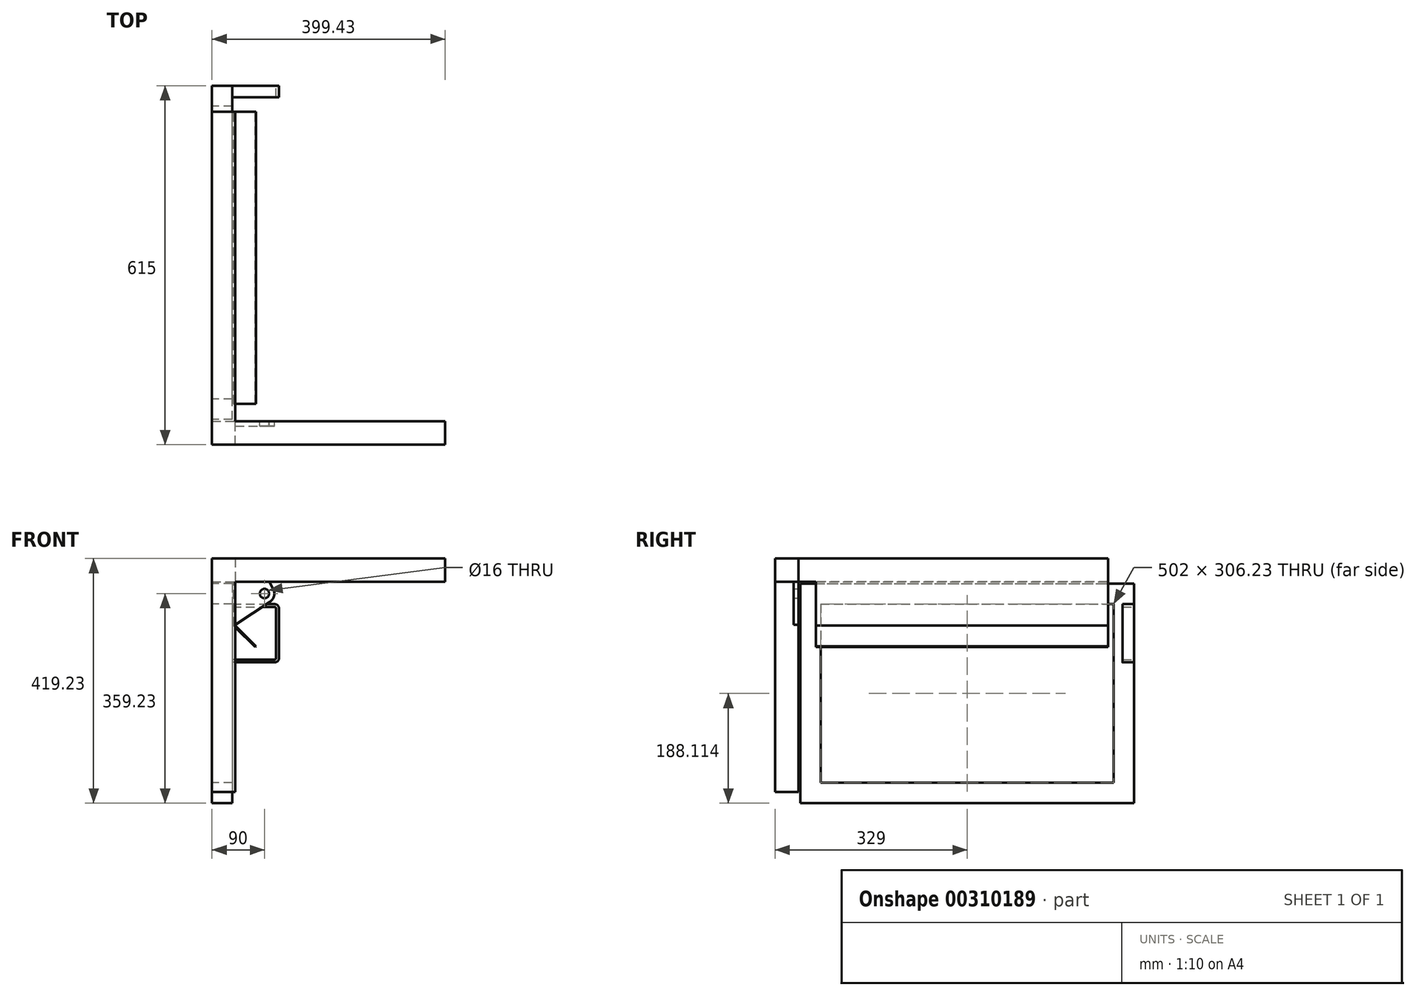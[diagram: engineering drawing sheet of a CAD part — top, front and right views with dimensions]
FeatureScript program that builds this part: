
annotation { "Feature Type Name" : "Feature", "Feature Type Description" : "" }
export const myFeature = defineFeature(function(context is Context, id is Id, definition is map)
    precondition{}
    {
        {
            var Q0;
            Q0=qCreatedBy(makeId("Front.planeOp"),FACE);
            var sketch = newSketch(context, id + "F0", { "sketchPlane" : qUnion([Q0])});
            skLineSegment(sketch, "E0.top", {"start": v(0, -400) * mm, "end": v(40, -400) * mm});
            skLineSegment(sketch, "E0.left", {"start": v(0, 0) * mm, "end": v(0, -400) * mm});
            skLineSegment(sketch, "E0.right", {"start": v(40, -40) * mm, "end": v(40, -400) * mm});
            skLineSegment(sketch, "E1.bottom", {"start": v(-0.57, 0) * mm, "end": v(399.43, 0) * mm});
            skLineSegment(sketch, "E1.top", {"start": v(40, -40) * mm, "end": v(399.43, -40) * mm});
            skLineSegment(sketch, "E1.right", {"start": v(399.43, 0) * mm, "end": v(399.43, -40) * mm});
            skSolve(sketch);
        }
        {
            var Q0;
            Q0 = qSketchRegion(id + "F0", true);
            extrude(context, id + "F1", {"entities" : qUnion([Q0]), "depth" : 40 * mm});
        }
        {
            var Q0;
            Q0=makeQuery(id+"F1.opExtrude","CAP_FACE",FACE,{"disambiguationData":[OSD([sQuery(id+"F0.wireOp",EDGE,"E0.top"),sQuery(id+"F0.wireOp",EDGE,"E0.left"),sQuery(id+"F0.wireOp",EDGE,"E0.right"),sQuery(id+"F0.wireOp",EDGE,"E1.bottom"),sQuery(id+"F0.wireOp",EDGE,"E1.top"),sQuery(id+"F0.wireOp",EDGE,"E1.right")])],"isStart":true});
            var sketch = newSketch(context, id + "F2", { "sketchPlane" : qUnion([Q0])});
            skLineSegment(sketch, "E2.bottom", {"start": v(0, 0) * mm, "end": v(-40, 0) * mm});
            skLineSegment(sketch, "E2.top", {"start": v(0, -40) * mm, "end": v(-40, -40) * mm});
            skLineSegment(sketch, "E2.left", {"start": v(0, 0) * mm, "end": v(0, -40) * mm});
            skLineSegment(sketch, "E2.right", {"start": v(-40, 0) * mm, "end": v(-40, -40) * mm});
            skSolve(sketch);
        }
        {
            var Q0;
            Q0 = qSketchRegion(id + "F2", true);
            extrude(context, id + "F3", {"entities" : qUnion([Q0]), "operationType" : NewBodyOperationType.ADD, "depth" : 530 * mm});
        }
        {
            var Q0;
            {var subQ0=sQuery(id+"F0.wireOp",EDGE,"E1.bottom");var subQ1=sQuery(id+"F0.wireOp",EDGE,"E0.right");var subQ2=sQuery(id+"F0.wireOp",EDGE,"E1.top");var subQ3=sQuery(id+"F0.wireOp",EDGE,"E1.right");var subQ4=makeQuery(id+"F1.opExtrude","CAP_FACE",FACE,{"disambiguationData":[OSD([sQuery(id+"F0.wireOp",EDGE,"E0.top"),sQuery(id+"F0.wireOp",EDGE,"E0.left"),subQ1,subQ0,subQ2,subQ3])],"isStart":true});Q0=makeQuery(id+"F3.boolean.opBoolean","SPLIT",FACE,{"disambiguationData":[TD([makeQuery(id+"F1.opExtrude","SWEPT_FACE",FACE,{"disambiguationData":[OSD([subQ0])]})])],"derivedFrom":subQ4});}
            var sketch = newSketch(context, id + "F4", { "sketchPlane" : qUnion([Q0])});
            skCircle(sketch, "E3", {"center": v(-90, -60) * mm, "radius": 8 * mm});
            skArc(sketch, "E4", {"start": v(-104.87, -51.75) * mm, "mid": v(-106.51, -64.04) * mm, "end": v(-99.38, -74.18) * mm});
            skLineSegment(sketch, "E5", {"start": v(-40, -40) * mm, "end": v(-40, -113.47) * mm});
            skLineSegment(sketch, "E6", {"start": v(-40, -113.47) * mm, "end": v(-99.38, -74.18) * mm});
            skLineSegment(sketch, "E7", {"start": v(-40, -40) * mm, "end": v(-98.35, -40) * mm});
            skLineSegment(sketch, "E8", {"start": v(-98.35, -40) * mm, "end": v(-104.87, -51.75) * mm});
            skSolve(sketch);
        }
        {
            var Q0;
            Q0 = qSketchRegion(id + "F4", true);
            extrude(context, id + "F5", {"entities" : qUnion([Q0]), "operationType" : NewBodyOperationType.ADD, "oppositeDirection" : true, "depth" : 8 * mm});
        }
        {
            var Q0;
            Q0=makeQuery(id+"F3.opExtrude","SWEPT_FACE",FACE,{"disambiguationData":[OSD([sQuery(id+"F2.wireOp",EDGE,"E2.top")])]});
            var sketch = newSketch(context, id + "F6", { "sketchPlane" : qUnion([Q0])});
            skLineSegment(sketch, "E9.bottom", {"start": v(37, -530) * mm, "end": v(40, -530) * mm});
            skLineSegment(sketch, "E9.top", {"start": v(37, -30) * mm, "end": v(40, -30) * mm});
            skLineSegment(sketch, "E9.right", {"start": v(40, -530) * mm, "end": v(40, -30) * mm});
            skLineSegment(sketch, "E10", {"start": v(37, -30) * mm, "end": v(37, -530) * mm});
            skSolve(sketch);
        }
        {
            var Q0;
            Q0 = qSketchRegion(id + "F6", true);
            extrude(context, id + "F7", {"entities" : qUnion([Q0]), "operationType" : NewBodyOperationType.ADD, "depth" : 75 * mm});
        }
        {
            var Q0;
            Q0=makeQuery(id+"F7.boolean.opBoolean","MERGE",FACE,{"derivedFrom":[makeQuery(id+"F3.opExtrude","CAP_FACE",FACE,{"disambiguationData":[OSD([sQuery(id+"F2.wireOp",EDGE,"E2.bottom"),sQuery(id+"F2.wireOp",EDGE,"E2.top"),sQuery(id+"F2.wireOp",EDGE,"E2.left"),sQuery(id+"F2.wireOp",EDGE,"E2.right")])],"isStart":false}),makeQuery(id+"F7.opExtrude","SWEPT_FACE",FACE,{"disambiguationData":[OSD([sQuery(id+"F6.wireOp",EDGE,"E9.bottom")])]})]});
            var sketch = newSketch(context, id + "F8", { "sketchPlane" : qUnion([Q0])});
            skLineSegment(sketch, "E11", {"start": v(-40, -115) * mm, "end": v(-75.36, -150.36) * mm});
            skLineSegment(sketch, "E12", {"start": v(-75.36, -150.36) * mm, "end": v(-75.36, -150.36) * mm});
            skLineSegment(sketch, "E13", {"start": v(-40, -115) * mm, "end": v(-40, -115) * mm});
            skLineSegment(sketch, "E14", {"start": v(-40, -115) * mm, "end": v(-37, -115) * mm});
            skLineSegment(sketch, "E15", {"start": v(-37, -115) * mm, "end": v(-73.88, -151.88) * mm});
            skLineSegment(sketch, "E16", {"start": v(-73.88, -151.88) * mm, "end": v(-75.36, -150.36) * mm});
            skSolve(sketch);
        }
        {
            var Q0;
            Q0 = qSketchRegion(id + "F8", true);
            var Q1;
            Q1=makeQuery(id+"F7.opExtrude","SWEPT_FACE",FACE,{"disambiguationData":[OSD([sQuery(id+"F6.wireOp",EDGE,"E9.top")])]});
            extrude(context, id + "F9", {"entities" : qUnion([Q0]), "operationType" : NewBodyOperationType.ADD, "endBound" : BoundingType.UP_TO_SURFACE, "oppositeDirection" : true, "endBoundEntityFace" : qUnion([Q1]), "depth" : 25 * mm});
        }
        {
            var Q0;
            Q0=makeQuery(id+"F3.boolean.opBoolean","MERGE",FACE,{"derivedFrom":[makeQuery(id+"F1.opExtrude","SWEPT_FACE",FACE,{"disambiguationData":[OSD([sQuery(id+"F0.wireOp",EDGE,"E0.left")])]}),makeQuery(id+"F3.opExtrude","SWEPT_FACE",FACE,{"disambiguationData":[OSD([sQuery(id+"F2.wireOp",EDGE,"E2.left")])]})]});
            var sketch = newSketch(context, id + "F10", { "sketchPlane" : qUnion([Q0])});
            skLineSegment(sketch, "E17.bottom", {"start": v(-3, -43) * mm, "end": v(-575, -43) * mm});
            skLineSegment(sketch, "E17.top", {"start": v(-3, -419.23) * mm, "end": v(-575, -419.23) * mm});
            skLineSegment(sketch, "E17.left", {"start": v(-3, -43) * mm, "end": v(-3, -419.23) * mm});
            skLineSegment(sketch, "E17.right", {"start": v(-575, -43) * mm, "end": v(-575, -419.23) * mm});
            skLineSegment(sketch, "E18.0", {"start": v(-540, -78) * mm, "end": v(-540, -384.23) * mm});
            skLineSegment(sketch, "E18.1", {"start": v(-38, -78) * mm, "end": v(-540, -78) * mm});
            skLineSegment(sketch, "E18.2", {"start": v(-38, -78) * mm, "end": v(-38, -384.23) * mm});
            skLineSegment(sketch, "E18.3", {"start": v(-38, -384.23) * mm, "end": v(-540, -384.23) * mm});
            skSolve(sketch);
        }
        {
            var Q0;
            Q0 = qSketchRegion(id + "F10", true);
            extrude(context, id + "F11", {"entities" : qUnion([Q0]), "oppositeDirection" : true, "depth" : 35 * mm});
        }
        {
            var Q0;
            Q0=makeQuery(id+"F11.opExtrude","SWEPT_FACE",FACE,{"disambiguationData":[OSD([sQuery(id+"F10.wireOp",EDGE,"E17.right")])]});
            var sketch = newSketch(context, id + "F12", { "sketchPlane" : qUnion([Q0])});
            skLineSegment(sketch, "E19", {"start": v(-35, -78) * mm, "end": v(-107, -78) * mm});
            skLineSegment(sketch, "E20", {"start": v(-115, -86) * mm, "end": v(-115, -170) * mm});
            skLineSegment(sketch, "E21", {"start": v(-107, -178) * mm, "end": v(-35, -178) * mm});
            skPoint(sketch, "E22.visualSharp", {"position": v(-115, -78) * mm});
            skArc(sketch, "E22.filletArc", {"start": v(-107, -78) * mm, "mid": v(-112.66, -80.34) * mm, "end": v(-115, -86) * mm});
            skPoint(sketch, "E23.visualSharp", {"position": v(-115, -178) * mm});
            skArc(sketch, "E23.filletArc", {"start": v(-115, -170) * mm, "mid": v(-112.66, -175.66) * mm, "end": v(-107, -178) * mm});
            skLineSegment(sketch, "E24.0", {"start": v(-107, -173) * mm, "end": v(-35, -173) * mm});
            skLineSegment(sketch, "E24.1", {"start": v(-35, -83) * mm, "end": v(-107, -83) * mm});
            skArc(sketch, "E24.2", {"start": v(-107, -83) * mm, "mid": v(-109.12, -83.88) * mm, "end": v(-110, -86) * mm});
            skLineSegment(sketch, "E24.3", {"start": v(-110, -86) * mm, "end": v(-110, -170) * mm});
            skArc(sketch, "E24.4", {"start": v(-110, -170) * mm, "mid": v(-109.12, -172.12) * mm, "end": v(-107, -173) * mm});
            skLineSegment(sketch, "E25", {"start": v(-35, -78) * mm, "end": v(-35, -83) * mm});
            skLineSegment(sketch, "E26", {"start": v(-35, -173) * mm, "end": v(-35, -178) * mm});
            skSolve(sketch);
        }
        {
            var Q0;
            Q0 = qSketchRegion(id + "F12", true);
            extrude(context, id + "F13", {"entities" : qUnion([Q0]), "operationType" : NewBodyOperationType.ADD, "oppositeDirection" : true, "depth" : 20 * mm});
        }
    });
